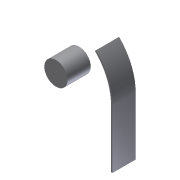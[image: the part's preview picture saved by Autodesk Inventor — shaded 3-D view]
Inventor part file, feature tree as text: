
AUTODESK INVENTOR PART (.ipt)
format: ipt  version: 2012 (Build 160160000, 160)  size: 82,944 bytes
history: native  units: in
note: dims shown in document units (in); Inventor stores cm internally (conversion verified against a paired STEP export)
features: extrude x1, sketch x1
ambient origin geometry x8: Origin, YZ Plane, XZ Plane, XY Plane, X Axis, Y Axis, Z Axis, Center Point
bodies: Solid1 (feature_tree)
feature tree (2):
  extrude  "Extrusion1"  Depth=9.75in
  sketch  "Sketch1"  dims[d0=9.5in d1=9.75in d3=4.0in d4=10.0in d5=45.0deg d6=4.0in d7=0.0in]
